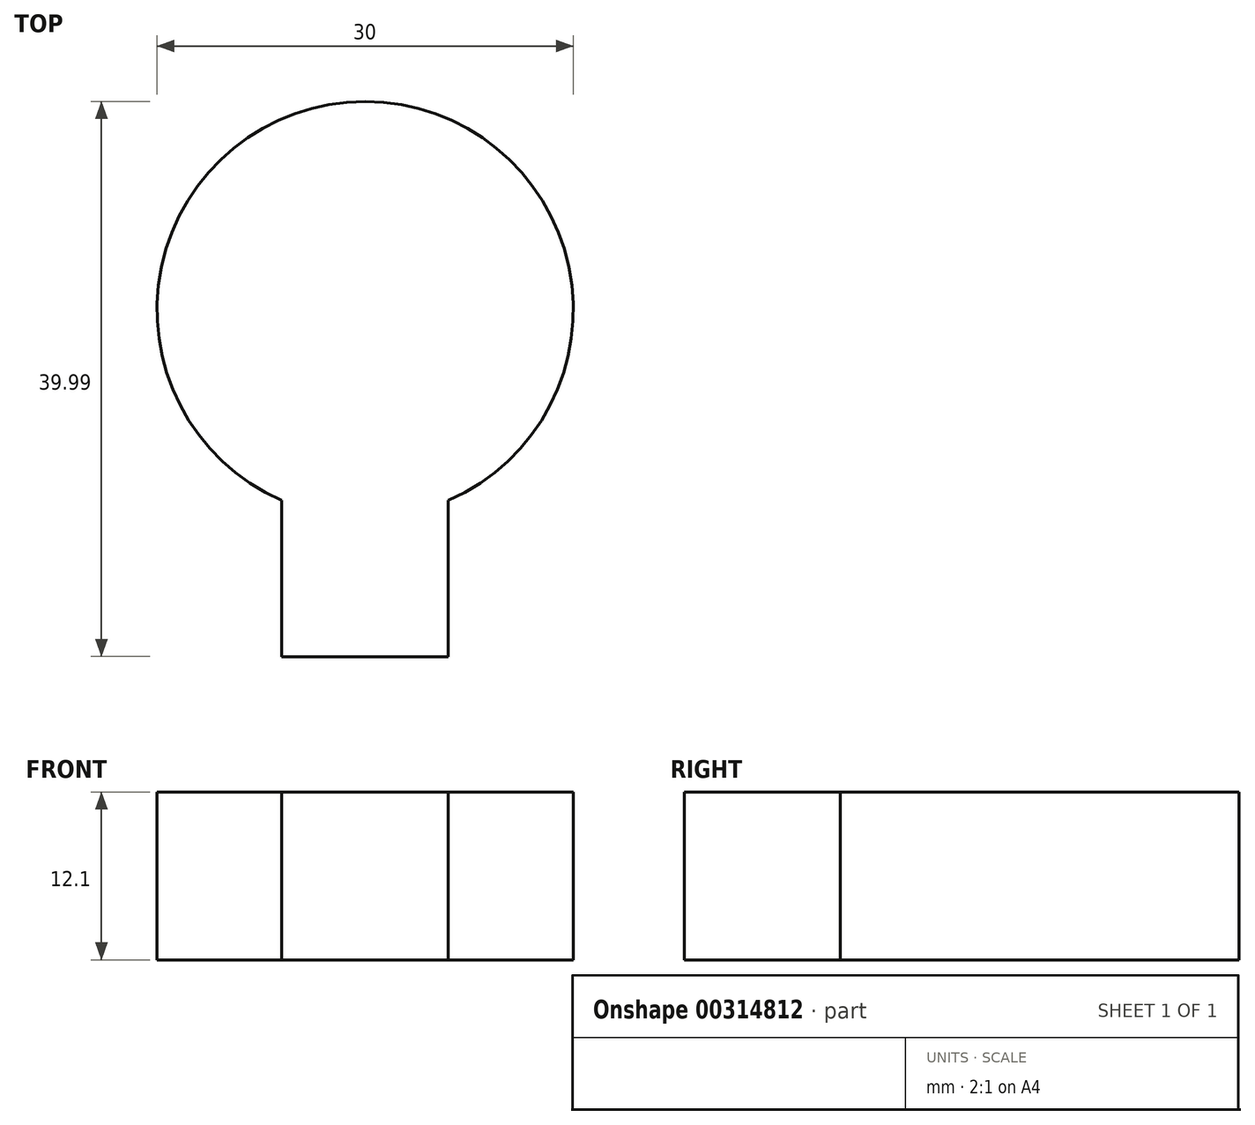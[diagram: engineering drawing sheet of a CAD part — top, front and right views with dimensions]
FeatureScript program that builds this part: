
annotation { "Feature Type Name" : "Feature", "Feature Type Description" : "" }
export const myFeature = defineFeature(function(context is Context, id is Id, definition is map)
    precondition{}
    {
        {
            var Q0;
            Q0=qCreatedBy(makeId("Top.planeOp"),FACE);
            var sketch = newSketch(context, id + "F0", { "sketchPlane" : qUnion([Q0])});
            skArc(sketch, "E0", {"start": v(6, -13.75) * mm, "mid": v(0, 15) * mm, "end": v(-6, -13.75) * mm});
            skLineSegment(sketch, "E1", {"start": v(0, 0) * mm, "end": v(0, -25) * mm, "construction": true});
            skLineSegment(sketch, "E2", {"start": v(0, -25) * mm, "end": v(-6, -25) * mm});
            skLineSegment(sketch, "E3", {"start": v(0, -25) * mm, "end": v(6, -25) * mm});
            skLineSegment(sketch, "E4", {"start": v(-6, -25) * mm, "end": v(-6, -13.75) * mm});
            skLineSegment(sketch, "E5", {"start": v(6, -25) * mm, "end": v(6, -13.75) * mm});
            skSolve(sketch);
        }
        {
            var Q0;
            Q0=makeQuery(id+"F0.imprint","IMPRINT",FACE,{"disambiguationData":[TD([[makeQuery(id+"F0.imprint","IMPRINT",EDGE,{"derivedFrom":sQuery(id+"F0.wireOp",EDGE,"E0")}),1.0]])]});
            extrude(context, id + "F1", {"entities" : qUnion([Q0]), "depth" : 12.1 * mm});
        }
    });
